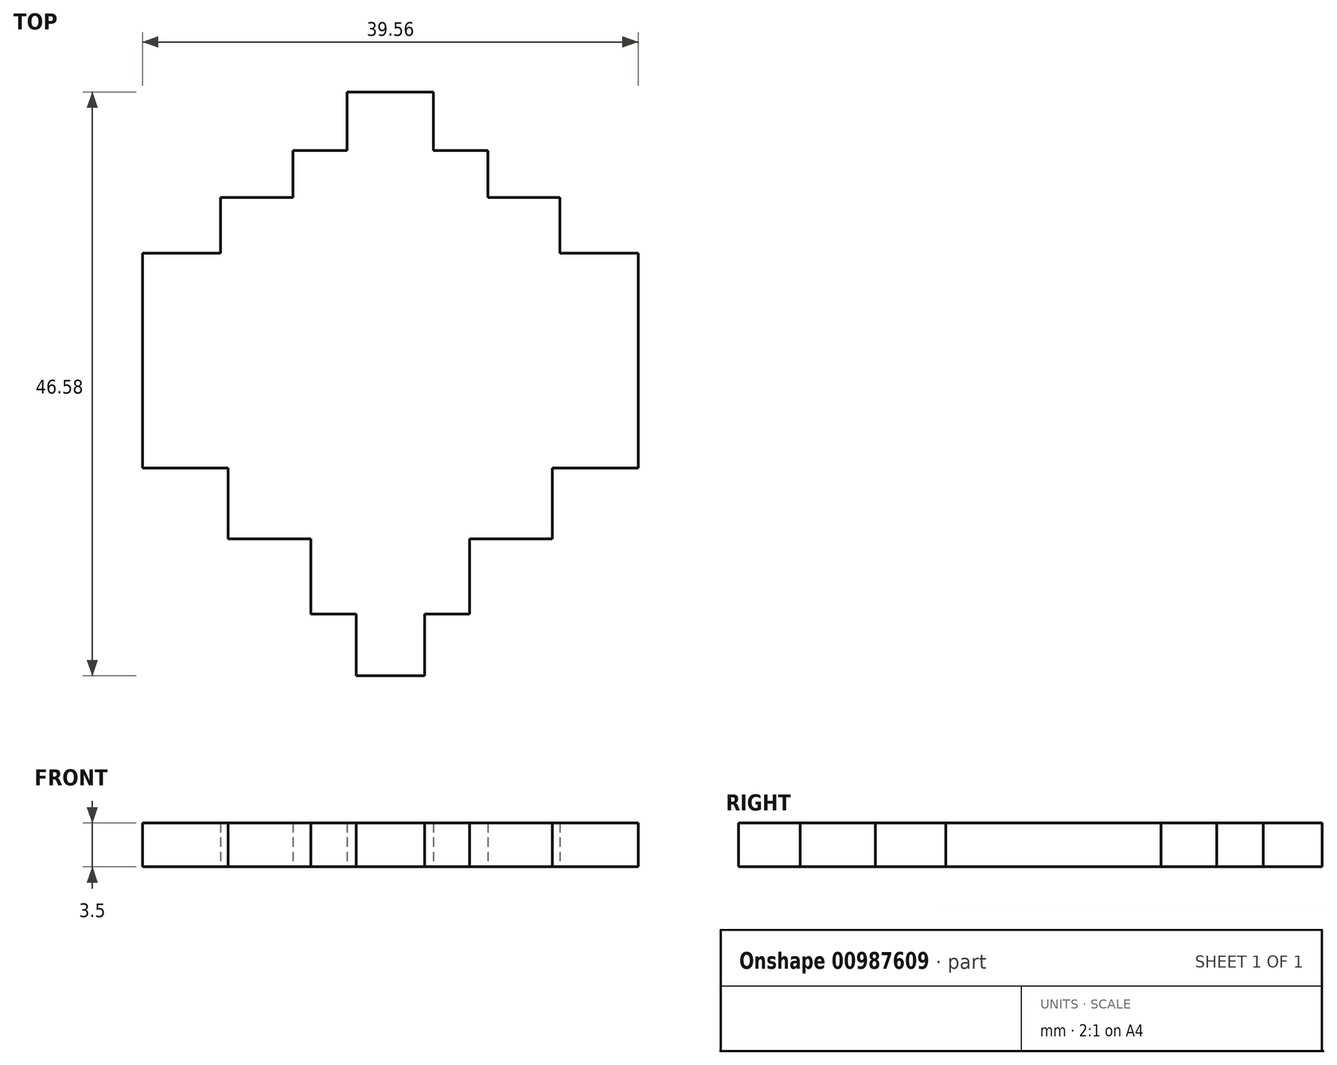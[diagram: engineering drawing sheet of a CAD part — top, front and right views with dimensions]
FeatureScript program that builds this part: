
annotation { "Feature Type Name" : "Feature", "Feature Type Description" : "" }
export const myFeature = defineFeature(function(context is Context, id is Id, definition is map)
    precondition{}
    {
        {
            var Q0;
            Q0=qCreatedBy(makeId("Top.planeOp"),FACE);
            var sketch = newSketch(context, id + "F0", { "sketchPlane" : qUnion([Q0])});
            skLineSegment(sketch, "E0", {"start": v(-19.87, 0) * mm, "end": v(17.63, 0) * mm, "construction": true});
            skLineSegment(sketch, "E1", {"start": v(0, 0) * mm, "end": v(0, 43.5) * mm, "construction": true});
            skSolve(sketch);
        }
        {
            var Q0;
            Q0=qCreatedBy(makeId("Top.planeOp"),FACE);
            var sketch = newSketch(context, id + "F1", { "sketchPlane" : qUnion([Q0])});
            skLineSegment(sketch, "E2", {"start": v(-19.78, 0) * mm, "end": v(-19.78, 7.5) * mm});
            skLineSegment(sketch, "E3", {"start": v(-19.78, 7.5) * mm, "end": v(-13.54, 7.5) * mm});
            skLineSegment(sketch, "E4", {"start": v(-13.54, 7.5) * mm, "end": v(-13.54, 11.95) * mm});
            skLineSegment(sketch, "E5", {"start": v(-13.54, 11.95) * mm, "end": v(-7.78, 11.95) * mm});
            skLineSegment(sketch, "E6", {"start": v(-7.78, 11.95) * mm, "end": v(-7.78, 15.67) * mm});
            skLineSegment(sketch, "E7", {"start": v(-7.78, 15.67) * mm, "end": v(-3.45, 15.67) * mm});
            skLineSegment(sketch, "E8", {"start": v(-3.45, 15.67) * mm, "end": v(-3.45, 20.35) * mm});
            skLineSegment(sketch, "E9", {"start": v(-3.45, 20.35) * mm, "end": v(0, 20.35) * mm});
            skLineSegment(sketch, "E10", {"start": v(-19.78, 0) * mm, "end": v(-19.78, -9.66) * mm});
            skLineSegment(sketch, "E11", {"start": v(-19.78, -9.66) * mm, "end": v(-12.94, -9.66) * mm});
            skLineSegment(sketch, "E12", {"start": v(-12.94, -9.66) * mm, "end": v(-12.94, -15.3) * mm});
            skLineSegment(sketch, "E13", {"start": v(-12.94, -15.3) * mm, "end": v(-6.33, -15.3) * mm});
            skLineSegment(sketch, "E14", {"start": v(-6.33, -15.3) * mm, "end": v(-6.33, -21.31) * mm});
            skLineSegment(sketch, "E15", {"start": v(-6.33, -21.31) * mm, "end": v(-2.73, -21.31) * mm});
            skLineSegment(sketch, "E16", {"start": v(-2.73, -21.31) * mm, "end": v(-2.73, -26.23) * mm});
            skLineSegment(sketch, "E17", {"start": v(-2.73, -26.23) * mm, "end": v(0, -26.23) * mm});
            skLineSegment(sketch, "E18.MirrorCS", {"start": v(3.45, 20.35) * mm, "end": v(0, 20.35) * mm});
            skLineSegment(sketch, "E19.MirrorCS", {"start": v(3.45, 15.67) * mm, "end": v(3.45, 20.35) * mm});
            skLineSegment(sketch, "E20.MirrorCS", {"start": v(7.78, 15.67) * mm, "end": v(3.45, 15.67) * mm});
            skLineSegment(sketch, "E21.MirrorCS", {"start": v(7.78, 11.95) * mm, "end": v(7.78, 15.67) * mm});
            skLineSegment(sketch, "E22.MirrorCS", {"start": v(13.54, 11.95) * mm, "end": v(7.78, 11.95) * mm});
            skLineSegment(sketch, "E23.MirrorCS", {"start": v(13.54, 7.5) * mm, "end": v(13.54, 11.95) * mm});
            skLineSegment(sketch, "E24.MirrorCS", {"start": v(19.78, 7.5) * mm, "end": v(13.54, 7.5) * mm});
            skLineSegment(sketch, "E25.MirrorCS", {"start": v(19.78, 0) * mm, "end": v(19.78, 7.5) * mm});
            skLineSegment(sketch, "E26.MirrorCS", {"start": v(19.78, 0) * mm, "end": v(19.78, -9.66) * mm});
            skLineSegment(sketch, "E27.MirrorCS", {"start": v(19.78, -9.66) * mm, "end": v(12.94, -9.66) * mm});
            skLineSegment(sketch, "E28.MirrorCS", {"start": v(12.94, -9.66) * mm, "end": v(12.94, -15.3) * mm});
            skLineSegment(sketch, "E29.MirrorCS", {"start": v(12.94, -15.3) * mm, "end": v(6.33, -15.3) * mm});
            skLineSegment(sketch, "E30.MirrorCS", {"start": v(6.33, -15.3) * mm, "end": v(6.33, -21.31) * mm});
            skLineSegment(sketch, "E31.MirrorCS", {"start": v(6.33, -21.31) * mm, "end": v(2.73, -21.31) * mm});
            skLineSegment(sketch, "E32.MirrorCS", {"start": v(2.73, -21.31) * mm, "end": v(2.73, -26.23) * mm});
            skLineSegment(sketch, "E33.MirrorCS", {"start": v(2.73, -26.23) * mm, "end": v(0, -26.23) * mm});
            skSolve(sketch);
        }
        {
            var Q0;
            Q0 = qSketchRegion(id + "F1", true);
            extrude(context, id + "F2", {"entities" : qUnion([Q0]), "depth" : 3.5 * mm, "offsetDistance" : 25 * mm});
        }
    });
